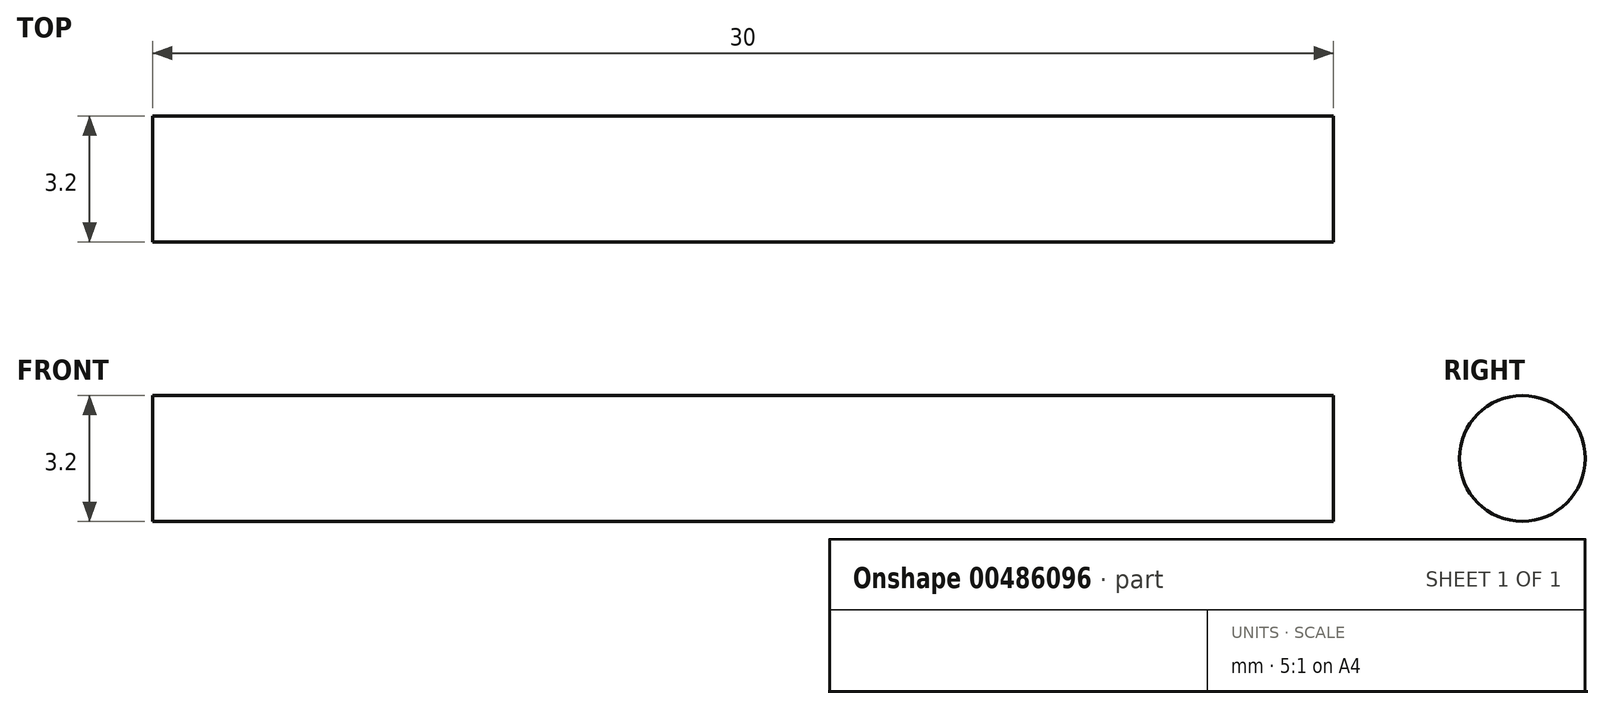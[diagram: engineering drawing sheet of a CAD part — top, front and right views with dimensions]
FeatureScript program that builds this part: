
annotation { "Feature Type Name" : "Feature", "Feature Type Description" : "" }
export const myFeature = defineFeature(function(context is Context, id is Id, definition is map)
    precondition{}
    {
        {
            var Q0;
            Q0=qCreatedBy(makeId("Right.planeOp"),FACE);
            var sketch = newSketch(context, id + "F0", { "sketchPlane" : qUnion([Q0])});
            skCircle(sketch, "E0", {"center": v(72, 65) * mm, "radius": 1.6 * mm});
            skCircle(sketch, "E1", {"center": v(83, 37) * mm, "radius": 10 * mm});
            skCircle(sketch, "E2", {"center": v(83, 52.56) * mm, "radius": 1.6 * mm});
            skCircle(sketch, "E3", {"center": v(98.56, 21.44) * mm, "radius": 1.75 * mm});
            skCircle(sketch, "E4", {"center": v(67.44, 52.56) * mm, "radius": 1.75 * mm});
            skCircle(sketch, "E5", {"center": v(151, -99.5) * mm, "radius": 1.6 * mm});
            skCircle(sketch, "E6", {"center": v(67.44, 21.44) * mm, "radius": 1.75 * mm});
            skCircle(sketch, "E7", {"center": v(67.45, 37) * mm, "radius": 1.6 * mm});
            skArc(sketch, "E8", {"start": v(191, -49.63) * mm, "mid": v(188.8, -32.58) * mm, "end": v(182.31, -16.66) * mm});
            skLineSegment(sketch, "E9", {"start": v(191, -49.63) * mm, "end": v(191, -122.08) * mm});
            skCircle(sketch, "E10", {"center": v(151, -49.5) * mm, "radius": 1.6 * mm});
            skArc(sketch, "E11", {"start": v(181.08, -132) * mm, "mid": v(188.1, -129.1) * mm, "end": v(191, -122.08) * mm});
            skCircle(sketch, "E12", {"center": v(94, 87) * mm, "radius": 1.6 * mm});
            skCircle(sketch, "E13", {"center": v(-171, -49.5) * mm, "radius": 1.6 * mm});
            skLineSegment(sketch, "E14", {"start": v(-181.08, -132) * mm, "end": v(83, -132) * mm});
            skCircle(sketch, "E15", {"center": v(171, -99.5) * mm, "radius": 1.6 * mm});
            skLineSegment(sketch, "E16", {"start": v(112.88, 106) * mm, "end": v(105.63, 118.8) * mm});
            skCircle(sketch, "E17", {"center": v(-171, -99.5) * mm, "radius": 1.6 * mm});
            skCircle(sketch, "E18", {"center": v(94, 9) * mm, "radius": 1.6 * mm});
            skCircle(sketch, "E19", {"center": v(83, -2) * mm, "radius": 6 * mm});
            skArc(sketch, "E20", {"start": v(-174.97, -22.14) * mm, "mid": v(-186.72, -34.4) * mm, "end": v(-191, -50.82) * mm});
            skArc(sketch, "E21", {"start": v(-191, -122.08) * mm, "mid": v(-188.1, -129.1) * mm, "end": v(-181.08, -132) * mm});
            skLineSegment(sketch, "E22", {"start": v(83, -132) * mm, "end": v(181.08, -132) * mm});
            skCircle(sketch, "E23", {"center": v(-171, -114.5) * mm, "radius": 1.6 * mm});
            skCircle(sketch, "E24", {"center": v(171, -49.5) * mm, "radius": 1.6 * mm});
            skArc(sketch, "E25", {"start": v(105.63, 118.8) * mm, "mid": v(89.49, 131.18) * mm, "end": v(69.38, 128.15) * mm});
            skLineSegment(sketch, "E26", {"start": v(-191, -122.08) * mm, "end": v(-191, -50.82) * mm});
            skCircle(sketch, "E27", {"center": v(83, 76) * mm, "radius": 6 * mm});
            skCircle(sketch, "E28", {"center": v(83, 21.45) * mm, "radius": 1.6 * mm});
            skCircle(sketch, "E29", {"center": v(-151, -49.5) * mm, "radius": 1.6 * mm});
            skCircle(sketch, "E30", {"center": v(-151, -64.5) * mm, "radius": 1.6 * mm});
            skLineSegment(sketch, "E31", {"start": v(-174.97, -22.14) * mm, "end": v(69.38, 128.15) * mm});
            skCircle(sketch, "E32", {"center": v(72, -13) * mm, "radius": 1.6 * mm});
            skCircle(sketch, "E33", {"center": v(151, -114.5) * mm, "radius": 1.6 * mm});
            skCircle(sketch, "E34", {"center": v(98.55, 37) * mm, "radius": 1.6 * mm});
            skCircle(sketch, "E35", {"center": v(113.72, 81.17) * mm, "radius": 4 * mm});
            skLineSegment(sketch, "E36", {"start": v(182.31, -16.66) * mm, "end": v(112.88, 106) * mm});
            skCircle(sketch, "E37", {"center": v(-171, -64.5) * mm, "radius": 1.6 * mm});
            skCircle(sketch, "E38", {"center": v(171, -114.5) * mm, "radius": 1.6 * mm});
            skCircle(sketch, "E39", {"center": v(-151, -99.5) * mm, "radius": 1.6 * mm});
            skCircle(sketch, "E40", {"center": v(171, -64.5) * mm, "radius": 1.6 * mm});
            skCircle(sketch, "E41", {"center": v(-151, -114.5) * mm, "radius": 1.6 * mm});
            skCircle(sketch, "E42", {"center": v(162.99, -5.86) * mm, "radius": 4 * mm});
            skCircle(sketch, "E43", {"center": v(98.56, 52.56) * mm, "radius": 1.75 * mm});
            skCircle(sketch, "E44", {"center": v(151, -64.5) * mm, "radius": 1.6 * mm});
            skSolve(sketch);
        }
        {
            var Q0;
            Q0=makeQuery(id+"F0.imprint","IMPRINT",FACE,{"disambiguationData":[TD([[makeQuery(id+"F0.imprint","IMPRINT",EDGE,{"derivedFrom":sQuery(id+"F0.wireOp",EDGE,"E0")}),1.0]])]});
            extrude(context, id + "F1", {"entities" : qUnion([Q0]), "depth" : 30 * mm});
        }
    });
